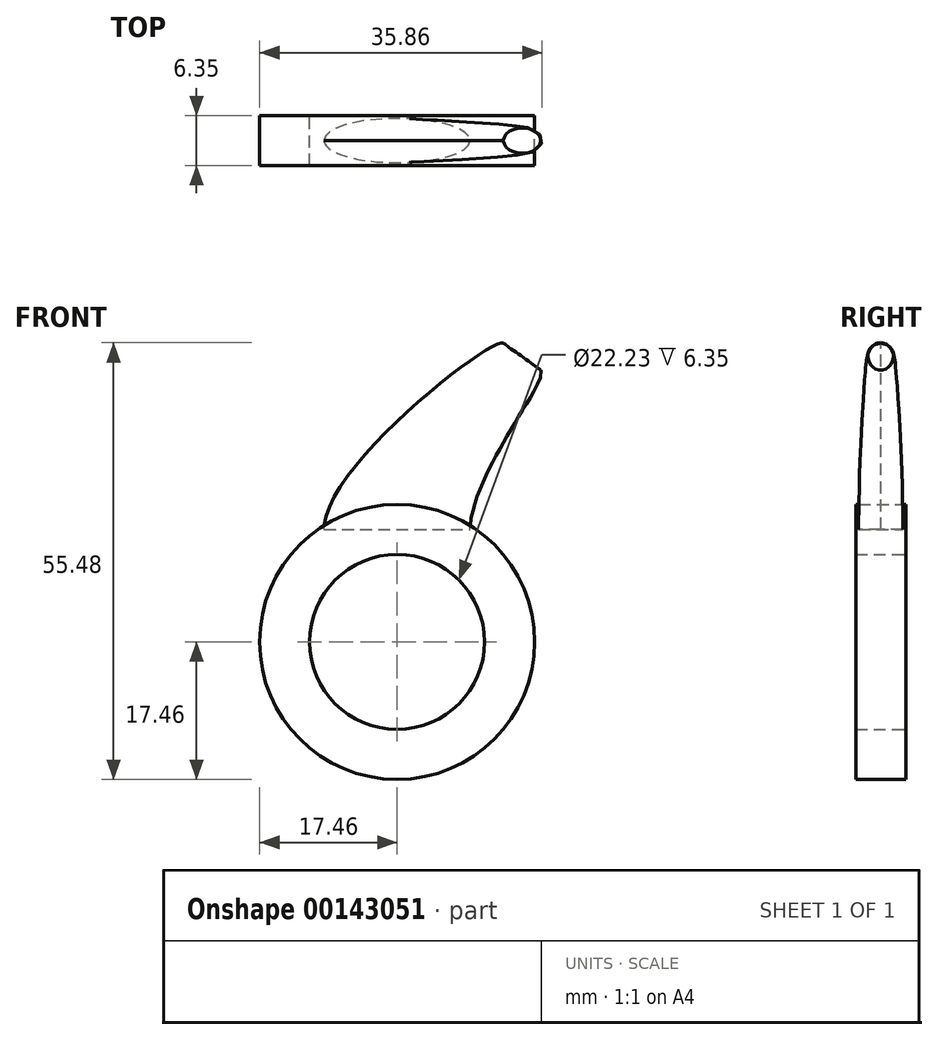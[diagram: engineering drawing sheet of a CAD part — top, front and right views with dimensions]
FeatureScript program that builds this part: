
annotation { "Feature Type Name" : "Feature", "Feature Type Description" : "" }
export const myFeature = defineFeature(function(context is Context, id is Id, definition is map)
    precondition{}
    {
        {
            var Q0;
            Q0=qCreatedBy(makeId("Front.planeOp"),FACE);
            var sketch = newSketch(context, id + "F0", { "sketchPlane" : qUnion([Q0])});
            skCircle(sketch, "E0", {"center": v(0, 0) * mm, "radius": 11.11 * mm});
            skCircle(sketch, "E1", {"center": v(0, 0) * mm, "radius": 17.46 * mm});
            skSolve(sketch);
        }
        {
            var Q0;
            Q0=makeQuery(id+"F0.imprint","IMPRINT",FACE,{"disambiguationData":[TD([[makeQuery(id+"F0.imprint","IMPRINT",EDGE,{"derivedFrom":sQuery(id+"F0.wireOp",EDGE,"E0")}),-1.0]])]});
            extrude(context, id + "F1", {"entities" : qUnion([Q0]), "depth" : 6.35 * mm});
        }
        {
            var Q0;
            Q0=qCreatedBy(makeId("Front.planeOp"),FACE);
            cPlane(context, id + "F2", {"entities" : qUnion([Q0]), "cplaneType" : CPlaneType.OFFSET, "offset" : 3.17 * mm, "width" : 152.4 * mm, "height" : 152.4 * mm});
        }
        {
            var Q0;
            Q0=qCreatedBy(makeId("Top.planeOp"),FACE);
            cPlane(context, id + "F3", {"entities" : qUnion([Q0]), "cplaneType" : CPlaneType.OFFSET, "offset" : 14.29 * mm, "width" : 152.4 * mm, "height" : 152.4 * mm});
        }
        {
            var Q0;
            Q0=qCreatedBy(makeId("Front.planeOp"),FACE);
            var sketch = newSketch(context, id + "F4", { "sketchPlane" : qUnion([Q0])});
            skLineSegment(sketch, "E2", {"start": v(0, 0) * mm, "end": v(0, 42.5) * mm, "construction": true});
            skArc(sketch, "E3", {"start": v(11.11, 39.69) * mm, "mid": v(3.05, 28.08) * mm, "end": v(0, 14.29) * mm, "construction": true});
            skArc(sketch, "E4", {"start": v(11.85, 38.03) * mm, "mid": v(7.9, 26.43) * mm, "end": v(9.53, 14.29) * mm});
            skLineSegment(sketch, "E5", {"start": v(0, 14.29) * mm, "end": v(9.53, 14.29) * mm});
            skLineSegment(sketch, "E6", {"start": v(11.11, 39.69) * mm, "end": v(12.35, 38.8) * mm, "construction": true});
            skArc(sketch, "E7", {"start": v(11.85, 38.03) * mm, "mid": v(11.92, 39.06) * mm, "end": v(11.11, 39.69) * mm});
            skArc(sketch, "E8", {"start": v(12.35, 38.8) * mm, "mid": v(12.1, 38.42) * mm, "end": v(11.85, 38.03) * mm, "construction": true});
            skArc(sketch, "E9", {"start": v(11.11, 39.69) * mm, "mid": v(2.54, 28.3) * mm, "end": v(0, 14.29) * mm});
            skSolve(sketch);
        }
        {
            var Q0;
            Q0=qCreatedBy(id+"F3.planeOp",FACE);
            var sketch = newSketch(context, id + "F5", { "sketchPlane" : qUnion([Q0])});
            skEllipse(sketch, "E10", {"center": v(0, -3.18) * mm, "majorRadius": 9.28 * mm, "minorRadius": 2.82 * mm, "majorAxis": v(-1, 0)});
            skSolve(sketch);
        }
        {
            var Q0;
            Q0=sQuery(id+"F4.wireOp",EDGE,"E6");
            cPlane(context, id + "F6", {"entities" : qUnion([Q0]), "cplaneType" : CPlaneType.LINE_ANGLE, "offset" : 25.4 * mm, "angle" : 90 * degree, "width" : 152.4 * mm, "height" : 152.4 * mm});
        }
        {
            var Q0;
            Q0=qCreatedBy(id+"F6.planeOp",FACE);
            var sketch = newSketch(context, id + "F7", { "sketchPlane" : qUnion([Q0])});
            skEllipse(sketch, "E11", {"center": v(-8.37, -3.18) * mm, "majorRadius": 2.98 * mm, "minorRadius": 1.64 * mm, "majorAxis": v(-1, 0)});
            skSolve(sketch);
        }
        {
            var Q0;
            Q0=qCreatedBy(id+"F2.planeOp",FACE);
            var sketch = newSketch(context, id + "F8", { "sketchPlane" : qUnion([Q0])});
            skArc(sketch, "E12", {"start": v(10.3, 39.9) * mm, "mid": v(1.6, 28.54) * mm, "end": v(0, 14.32) * mm});
            skSolve(sketch);
        }
        {
            var Q1;
            Q1 = qSketchRegion(id + "F5", true);
            var Q2;
            Q2 = qSketchRegion(id + "F7", true);
            var Q3;
            Q3=sQuery(id+"F8.wireOp",EDGE,"E12");
            loft(context, id + "F9", {"startCondition" : LoftEndDerivativeType.NORMAL_TO_PROFILE, "startMagnitude" : 1, "endCondition" : LoftEndDerivativeType.TANGENT_TO_PROFILE, "endMagnitude" : 1, "sheetProfilesArray" : [{ "sheetProfileEntities" : qUnion([Q1]) }, { "sheetProfileEntities" : qUnion([Q2]) }], "guidesArray" : [{ "guideEntities" : qUnion([Q3]), "guideDerivativeType" : LoftGuideDerivativeType.DEFAULT, "guideDerivativeMagnitude" : 1 }]});
        }
    });
